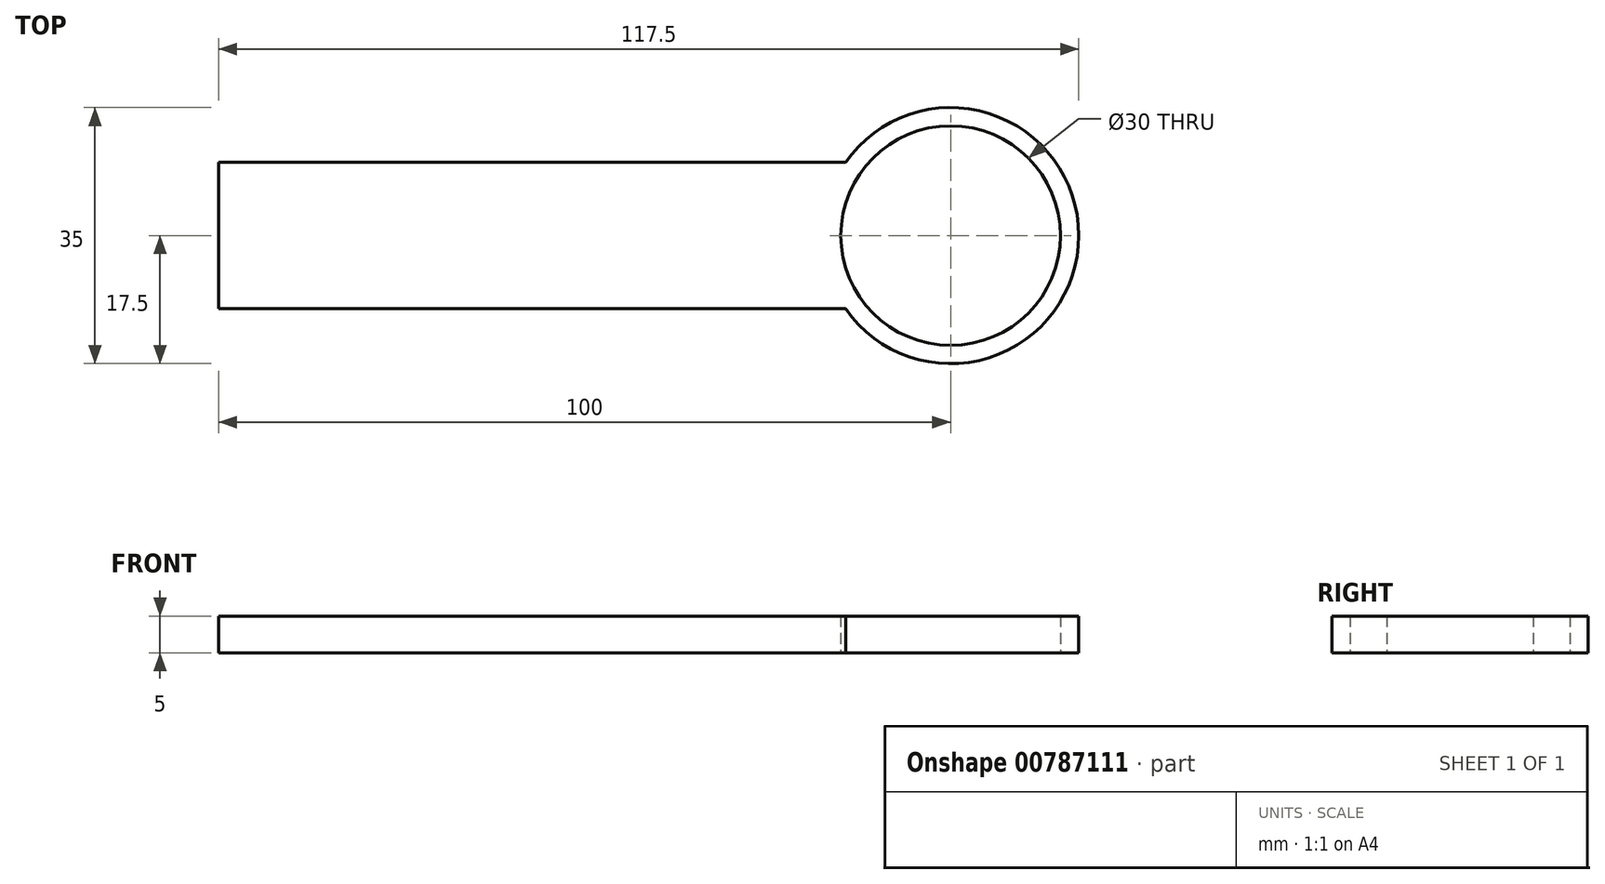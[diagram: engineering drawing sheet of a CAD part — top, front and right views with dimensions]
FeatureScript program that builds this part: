
annotation { "Feature Type Name" : "Feature", "Feature Type Description" : "" }
export const myFeature = defineFeature(function(context is Context, id is Id, definition is map)
    precondition{}
    {
        {
            var Q0;
            Q0=qCreatedBy(makeId("Top.planeOp"),FACE);
            var sketch = newSketch(context, id + "F0", { "sketchPlane" : qUnion([Q0])});
            skLineSegment(sketch, "E0.left", {"start": v(-50, 10) * mm, "end": v(-50, -10) * mm});
            skPoint(sketch, "E0.middle", {"position": v(0, 0) * mm});
            skCircle(sketch, "E1", {"center": v(50, 0) * mm, "radius": 17.5 * mm});
            skCircle(sketch, "E2", {"center": v(50, 0) * mm, "radius": 15 * mm});
            skLineSegment(sketch, "E3", {"start": v(-50, 10) * mm, "end": v(35.64, 10) * mm});
            skLineSegment(sketch, "E4", {"start": v(-50, -10) * mm, "end": v(35.64, -10) * mm});
            skSolve(sketch);
        }
        {
            var Q0;
            Q0 = qSketchRegion(id + "F0", true);
            extrude(context, id + "F1", {"entities" : qUnion([Q0]), "depth" : 5 * mm, "offsetDistance" : 25 * mm});
        }
    });
